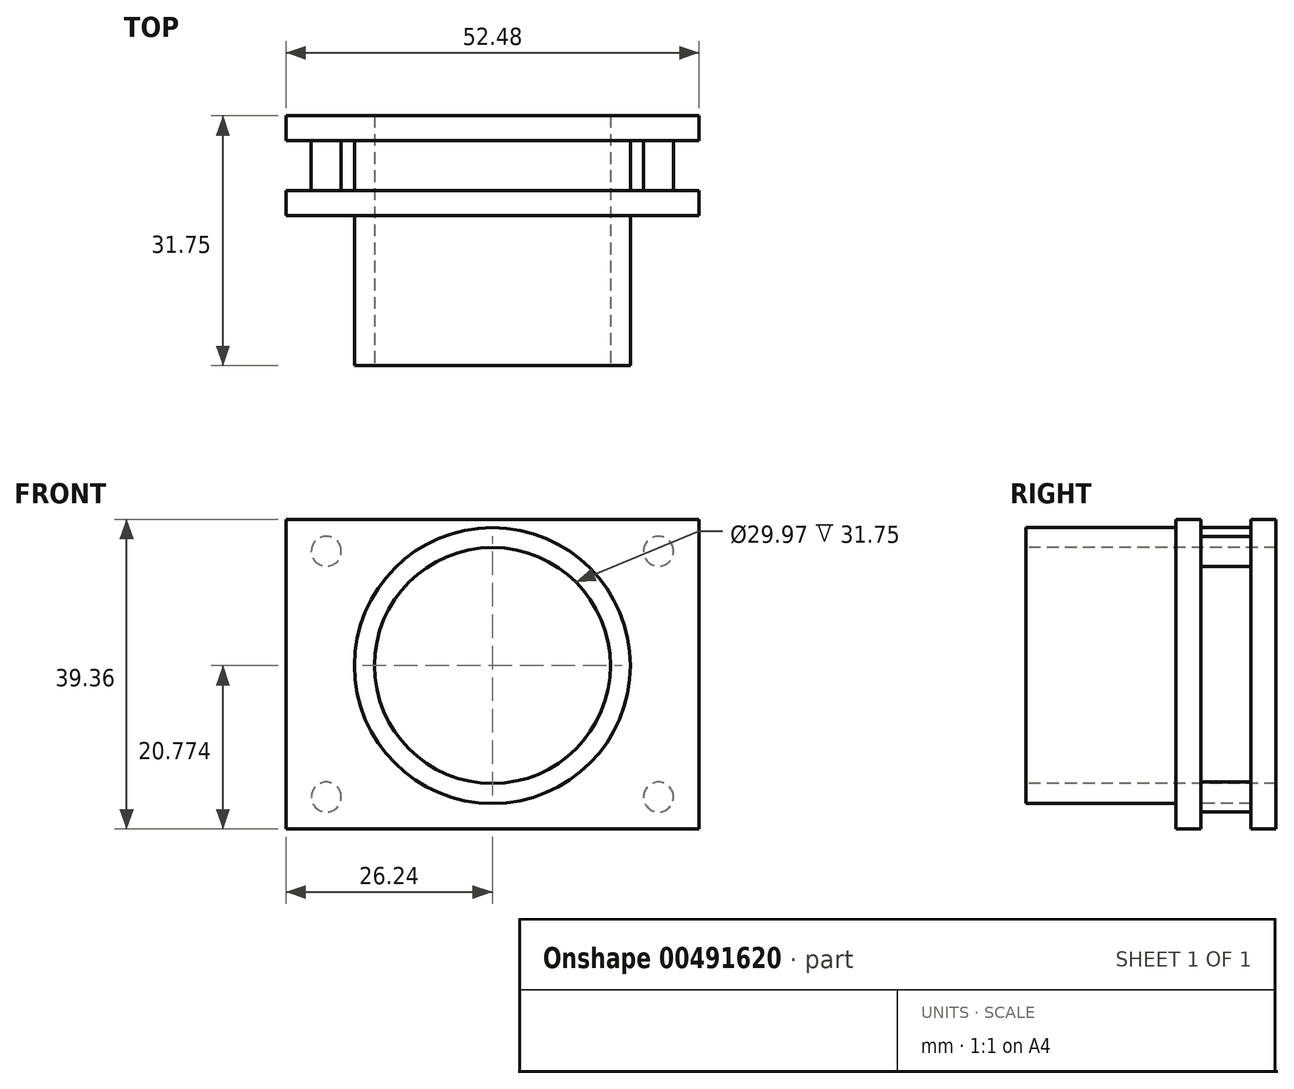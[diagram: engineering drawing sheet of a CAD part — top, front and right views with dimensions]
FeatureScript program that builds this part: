
annotation { "Feature Type Name" : "Feature", "Feature Type Description" : "" }
export const myFeature = defineFeature(function(context is Context, id is Id, definition is map)
    precondition{}
    {
        {
            var Q0;
            Q0=qCreatedBy(makeId("Front.planeOp"),FACE);
            var sketch = newSketch(context, id + "F0", { "sketchPlane" : qUnion([Q0])});
            skLineSegment(sketch, "E0.bottom", {"start": v(26.24, -19.68) * mm, "end": v(-26.24, -19.68) * mm});
            skLineSegment(sketch, "E0.top", {"start": v(26.24, 19.68) * mm, "end": v(-26.24, 19.68) * mm});
            skLineSegment(sketch, "E0.left", {"start": v(26.24, -19.68) * mm, "end": v(26.24, 19.68) * mm});
            skLineSegment(sketch, "E0.right", {"start": v(-26.24, -19.68) * mm, "end": v(-26.24, 19.68) * mm});
            skPoint(sketch, "E0.middle", {"position": v(0, 0) * mm});
            skSolve(sketch);
        }
        {
            var Q0;
            Q0 = qSketchRegion(id + "F0", true);
            extrude(context, id + "F1", {"entities" : qUnion([Q0]), "depth" : 12.7 * mm});
        }
        {
            var Q0;
            Q0=makeQuery(id+"F1.opExtrude","SWEPT_FACE",FACE,{"disambiguationData":[OSD([sQuery(id+"F0.wireOp",EDGE,"E0.right")])]});
            var sketch = newSketch(context, id + "F2", { "sketchPlane" : qUnion([Q0])});
            skLineSegment(sketch, "E1", {"start": v(0, 19.68) * mm, "end": v(6.35, 19.68) * mm});
            skLineSegment(sketch, "E2", {"start": v(6.35, -19.68) * mm, "end": v(12.7, -19.68) * mm});
            skLineSegment(sketch, "E3.bottom", {"start": v(3.18, 19.68) * mm, "end": v(9.53, 19.68) * mm});
            skLineSegment(sketch, "E3.top", {"start": v(3.18, -19.68) * mm, "end": v(9.53, -19.68) * mm});
            skLineSegment(sketch, "E3.left", {"start": v(3.18, 19.68) * mm, "end": v(3.18, -19.68) * mm});
            skLineSegment(sketch, "E3.right", {"start": v(9.53, 19.68) * mm, "end": v(9.53, -19.68) * mm});
            skSolve(sketch);
        }
        {
            var Q0;
            Q0 = qSketchRegion(id + "F2", true);
            extrude(context, id + "F3", {"entities" : qUnion([Q0]), "operationType" : NewBodyOperationType.REMOVE, "endBound" : BoundingType.THROUGH_ALL, "oppositeDirection" : true, "depth" : 25.4 * mm});
        }
        {
            var Q0;
            Q0=makeQuery(id+"F1.opExtrude","CAP_FACE",FACE,{"disambiguationData":[OSD([sQuery(id+"F0.wireOp",EDGE,"E0.bottom"),sQuery(id+"F0.wireOp",EDGE,"E0.top"),sQuery(id+"F0.wireOp",EDGE,"E0.left"),sQuery(id+"F0.wireOp",EDGE,"E0.right")])],"isStart":false});
            var sketch = newSketch(context, id + "F4", { "sketchPlane" : qUnion([Q0])});
            skLineSegment(sketch, "E4", {"start": v(-26.24, 19.68) * mm, "end": v(-21.1, 19.68) * mm});
            skLineSegment(sketch, "E5", {"start": v(-21.1, 19.68) * mm, "end": v(-21.1, -19.68) * mm});
            skLineSegment(sketch, "E6", {"start": v(26.24, 19.68) * mm, "end": v(21.1, 19.68) * mm});
            skLineSegment(sketch, "E7", {"start": v(21.1, 19.68) * mm, "end": v(21.1, -19.68) * mm});
            skLineSegment(sketch, "E8", {"start": v(-21.1, -19.68) * mm, "end": v(-21.1, -15.62) * mm});
            skLineSegment(sketch, "E9", {"start": v(-21.1, 19.68) * mm, "end": v(-21.1, 15.62) * mm});
            skLineSegment(sketch, "E10", {"start": v(21.1, 19.68) * mm, "end": v(21.1, 15.62) * mm});
            skLineSegment(sketch, "E11", {"start": v(21.1, -19.68) * mm, "end": v(21.1, -15.62) * mm});
            skCircle(sketch, "E12", {"center": v(-21.1, 15.62) * mm, "radius": 1.9 * mm});
            skCircle(sketch, "E13", {"center": v(-21.1, -15.62) * mm, "radius": 1.9 * mm});
            skCircle(sketch, "E14", {"center": v(21.1, -15.62) * mm, "radius": 1.9 * mm});
            skCircle(sketch, "E15", {"center": v(21.1, 15.62) * mm, "radius": 1.9 * mm});
            skCircle(sketch, "E16", {"center": v(0, 1.1) * mm, "radius": 17.52 * mm});
            skCircle(sketch, "E17", {"center": v(0, 1.1) * mm, "radius": 14.98 * mm});
            skSolve(sketch);
        }
        {
            var Q0;
            Q0 = qSketchRegion(id + "F4", true);
            extrude(context, id + "F5", {"entities" : qUnion([Q0]), "operationType" : NewBodyOperationType.ADD, "oppositeDirection" : true, "depth" : 12.7 * mm});
        }
        {
            var Q0;
            Q0=makeQuery(id+"F4.imprint","IMPRINT",FACE,{"disambiguationData":[TD([[makeQuery(id+"F4.imprint","IMPRINT",EDGE,{"derivedFrom":sQuery(id+"F4.wireOp",EDGE,"E16")}),1.0]])]});
            extrude(context, id + "F6", {"entities" : qUnion([Q0]), "operationType" : NewBodyOperationType.ADD, "depth" : 19.05 * mm});
        }
        {
            var Q0;
            Q0=makeQuery(id+"F4.imprint","IMPRINT",FACE,{"disambiguationData":[TD([[makeQuery(id+"F4.imprint","IMPRINT",EDGE,{"derivedFrom":sQuery(id+"F4.wireOp",EDGE,"E17")}),1.0]])]});
            extrude(context, id + "F7", {"entities" : qUnion([Q0]), "operationType" : NewBodyOperationType.REMOVE, "oppositeDirection" : true, "depth" : 25.4 * mm});
        }
    });
